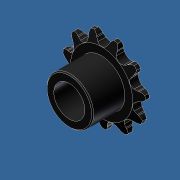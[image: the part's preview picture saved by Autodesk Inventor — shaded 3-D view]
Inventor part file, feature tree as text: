
AUTODESK INVENTOR PART (.ipt)
format: ipt  version: unknown  size: 599,040 bytes
history: native  units: in
note: dims shown in document units (in); Inventor stores cm internally (conversion verified against a paired STEP export)
features: extrude x2, sketch x2, other x1, imported_body x1
ambient origin geometry x8: Origin, YZ Plane, XZ Plane, XY Plane, X Axis, Y Axis, Z Axis, Center Point
feature tree (6):
  other  "Cut-Revolve1"
  imported_body  "Base1"
  extrude  "Extrusion2"  Depth=1.0in TaperAngle=0.0deg
  extrude  "Extrusion3"  Depth=1.0in TaperAngle=0.0deg
  sketch  "Sketch2"  dims[d3=0.375in d4=1.0in d5=0.0in]
  sketch  "Sketch3"  dims[d6=0.375in d7=1.0in d8=0.0in]
